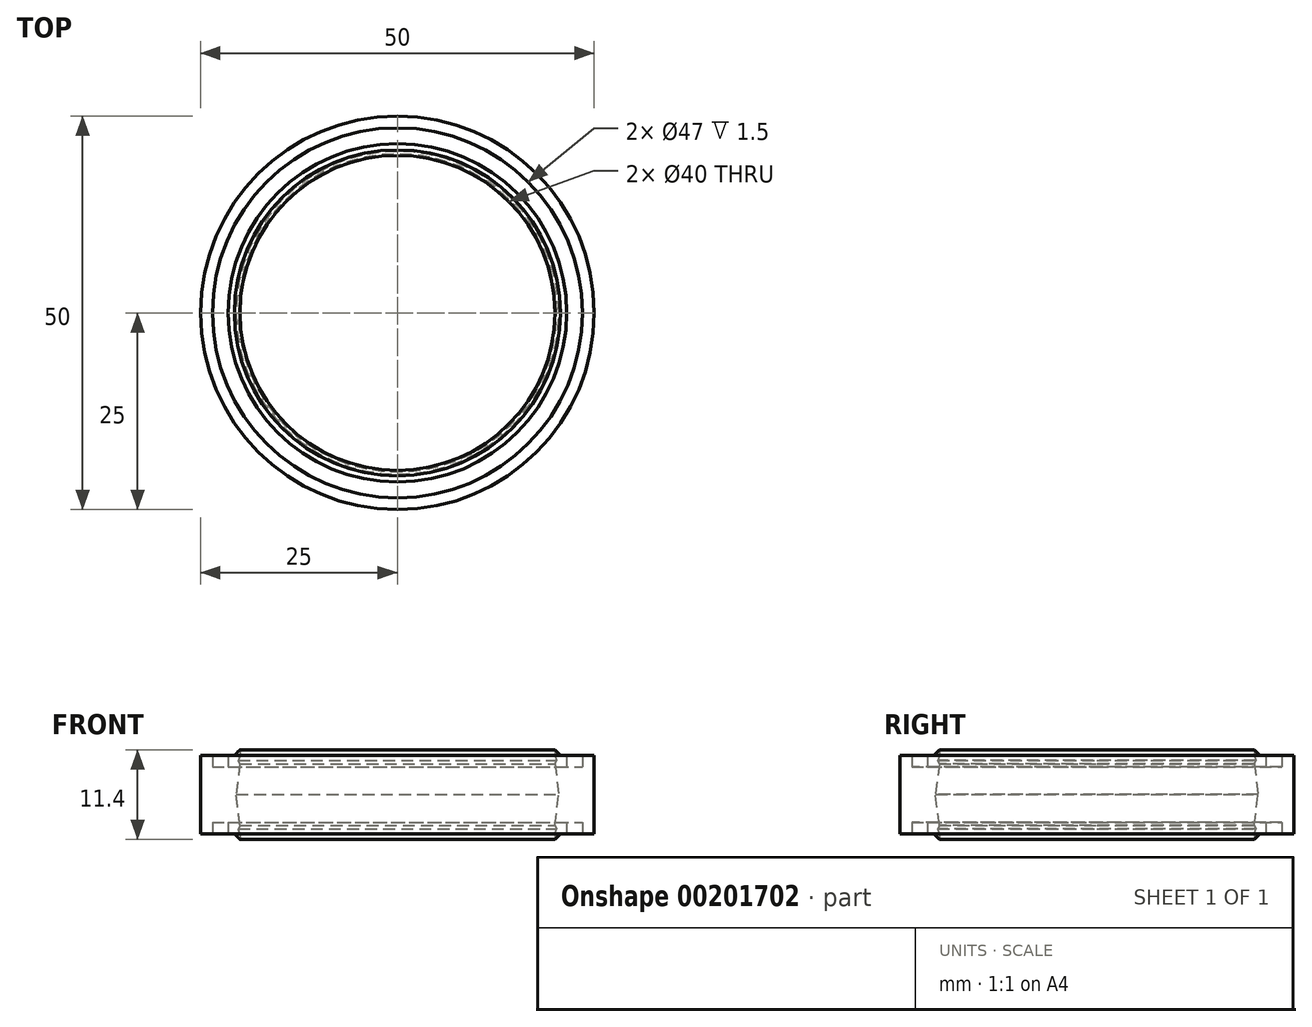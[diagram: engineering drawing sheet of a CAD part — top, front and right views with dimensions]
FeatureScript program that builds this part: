
annotation { "Feature Type Name" : "Feature", "Feature Type Description" : "" }
export const myFeature = defineFeature(function(context is Context, id is Id, definition is map)
    precondition{}
    {
        {
            var Q0;
            Q0=qCreatedBy(makeId("Front.planeOp"),FACE);
            var sketch = newSketch(context, id + "F0", { "sketchPlane" : qUnion([Q0])});
            skLineSegment(sketch, "E0", {"start": v(0, 0) * mm, "end": v(0, 37.02) * mm, "construction": true});
            skLineSegment(sketch, "E1.bottom", {"start": v(-25, 0) * mm, "end": v(-23.5, 0) * mm});
            skLineSegment(sketch, "E1.top", {"start": v(-25, 10) * mm, "end": v(-23.5, 10) * mm});
            skLineSegment(sketch, "E1.left", {"start": v(-25, 0) * mm, "end": v(-25, 10) * mm});
            skLineSegment(sketch, "E1.right", {"start": v(-20, -0.7) * mm, "end": v(-20, 0) * mm});
            skLineSegment(sketch, "E2", {"start": v(-20.7, 10) * mm, "end": v(-20, 10.7) * mm});
            skLineSegment(sketch, "E3", {"start": v(-25, 5) * mm, "end": v(-28.05, 5) * mm, "construction": true});
            skPoint(sketch, "E4.orphan", {"position": v(-20, 10) * mm});
            skLineSegment(sketch, "E5.MirrorCS", {"start": v(-20.7, 0) * mm, "end": v(-20, -0.7) * mm});
            skLineSegment(sketch, "E6.top", {"start": v(-23.5, 8.5) * mm, "end": v(-21.5, 8.5) * mm});
            skLineSegment(sketch, "E6.left", {"start": v(-23.5, 10) * mm, "end": v(-23.5, 8.5) * mm});
            skLineSegment(sketch, "E6.right", {"start": v(-21.5, 10) * mm, "end": v(-21.5, 8.5) * mm});
            skLineSegment(sketch, "E7.trimOffspring", {"start": v(-21.5, 10) * mm, "end": v(-20.7, 10) * mm});
            skLineSegment(sketch, "E8", {"start": v(-20, 10) * mm, "end": v(-20.2, 9.37) * mm});
            skLineSegment(sketch, "E9", {"start": v(-20.2, 9.37) * mm, "end": v(-20, 8.9) * mm});
            skLineSegment(sketch, "E10", {"start": v(-20, 8.9) * mm, "end": v(-20.5, 5) * mm});
            skLineSegment(sketch, "E11.trimOffspring", {"start": v(-20, 10) * mm, "end": v(-20, 10.7) * mm});
            skLineSegment(sketch, "E12.MirrorCS", {"start": v(-20, 1.1) * mm, "end": v(-20.5, 5) * mm});
            skLineSegment(sketch, "E13.MirrorCS", {"start": v(-20, 0) * mm, "end": v(-20.2, 0.63) * mm});
            skLineSegment(sketch, "E14.MirrorCS", {"start": v(-20.2, 0.63) * mm, "end": v(-20, 1.1) * mm});
            skLineSegment(sketch, "E15.MirrorCS", {"start": v(-23.5, 1.5) * mm, "end": v(-21.5, 1.5) * mm});
            skLineSegment(sketch, "E16.MirrorCS", {"start": v(-23.5, 0) * mm, "end": v(-23.5, 1.5) * mm});
            skLineSegment(sketch, "E17.MirrorCS", {"start": v(-21.5, 0) * mm, "end": v(-21.5, 1.5) * mm});
            skLineSegment(sketch, "E18.trimOffspring", {"start": v(-21.5, 0) * mm, "end": v(-20.7, 0) * mm});
            skSolve(sketch);
        }
        {
            var Q0;
            Q0=makeQuery(id+"F0.imprint","IMPRINT",FACE,{"disambiguationData":[TD([[makeQuery(id+"F0.imprint","IMPRINT",EDGE,{"derivedFrom":sQuery(id+"F0.wireOp",EDGE,"E1.bottom")}),1.0]])]});
            var Q1;
            Q1=sQuery(id+"F0.wireOp",EDGE,"E0");
            revolve(context, id + "F1", {"entities" : qUnion([Q0]), "axis" : qUnion([Q1]), "revolveType" : RevolveType.FULL});
        }
    });
